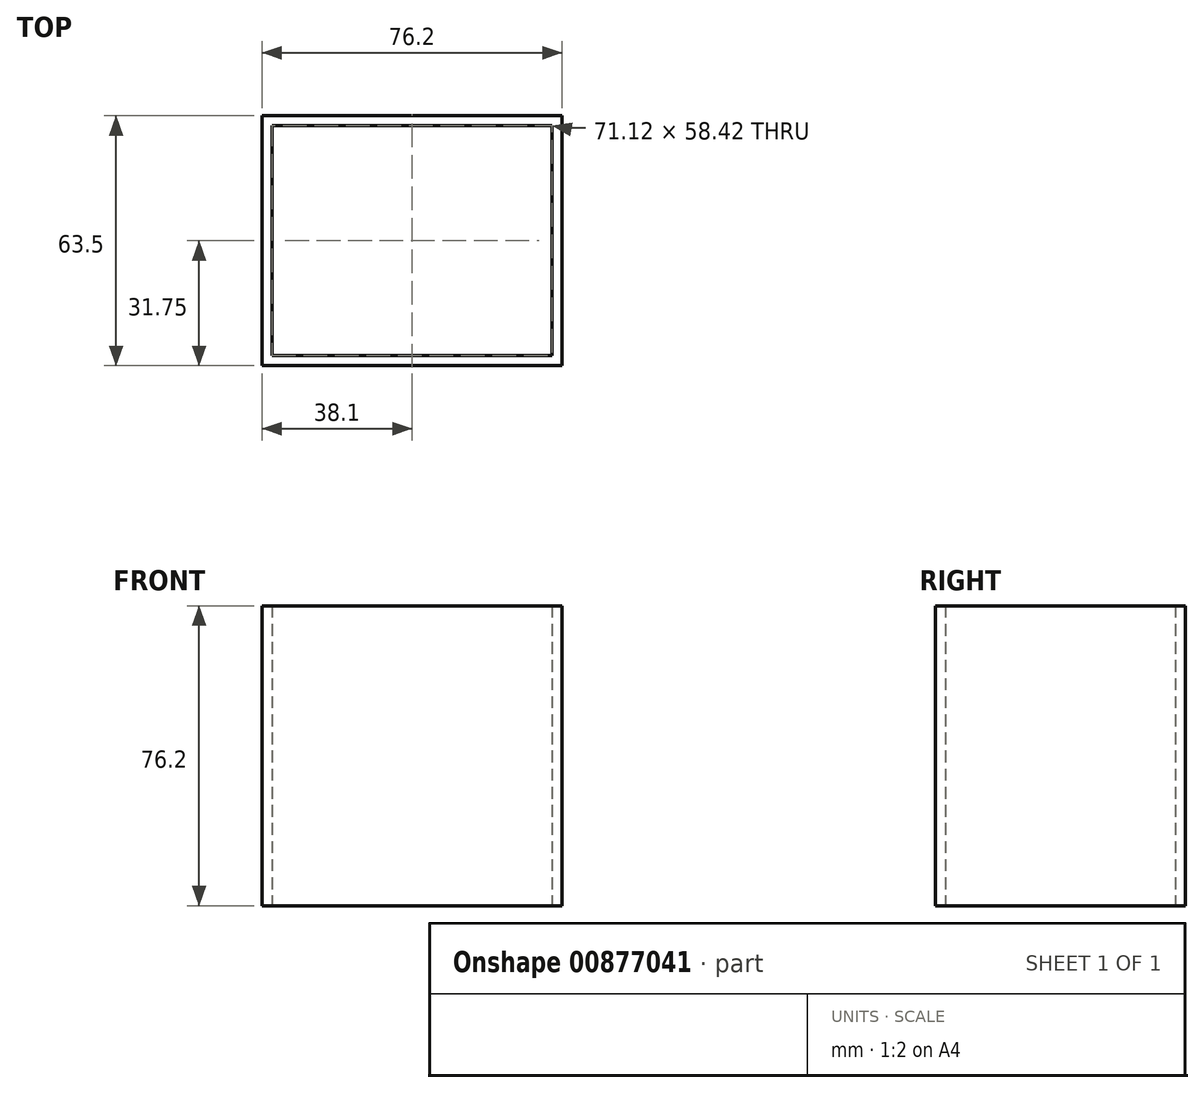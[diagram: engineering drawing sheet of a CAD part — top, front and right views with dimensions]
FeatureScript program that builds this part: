
annotation { "Feature Type Name" : "Feature", "Feature Type Description" : "" }
export const myFeature = defineFeature(function(context is Context, id is Id, definition is map)
    precondition{}
    {
        {
            var Q0;
            Q0=qCreatedBy(makeId("Top.planeOp"),FACE);
            var sketch = newSketch(context, id + "F0", { "sketchPlane" : qUnion([Q0])});
            skLineSegment(sketch, "E0.bottom", {"start": v(38.1, 31.75) * mm, "end": v(-38.1, 31.75) * mm});
            skLineSegment(sketch, "E0.top", {"start": v(38.1, -31.75) * mm, "end": v(-38.1, -31.75) * mm});
            skLineSegment(sketch, "E0.left", {"start": v(38.1, 31.75) * mm, "end": v(38.1, -31.75) * mm});
            skLineSegment(sketch, "E0.right", {"start": v(-38.1, 31.75) * mm, "end": v(-38.1, -31.75) * mm});
            skPoint(sketch, "E0.middle", {"position": v(0, 0) * mm});
            skLineSegment(sketch, "E1.bottom", {"start": v(35.56, 29.21) * mm, "end": v(-35.56, 29.2) * mm});
            skLineSegment(sketch, "E1.top", {"start": v(35.56, -29.21) * mm, "end": v(-35.56, -29.21) * mm});
            skLineSegment(sketch, "E1.left", {"start": v(35.56, 29.21) * mm, "end": v(35.56, -29.2) * mm});
            skLineSegment(sketch, "E1.right", {"start": v(-35.56, 29.2) * mm, "end": v(-35.56, -29.21) * mm});
            skSolve(sketch);
        }
        {
            var Q0;
            Q0=makeQuery(id+"F0.imprint","IMPRINT",FACE,{"disambiguationData":[TD([[makeQuery(id+"F0.imprint","IMPRINT",EDGE,{"derivedFrom":sQuery(id+"F0.wireOp",EDGE,"E0.bottom")}),1.0]])]});
            extrude(context, id + "F1", {"entities" : qUnion([Q0]), "depth" : 76.2 * mm, "offsetDistance" : 25.4 * mm});
        }
    });
